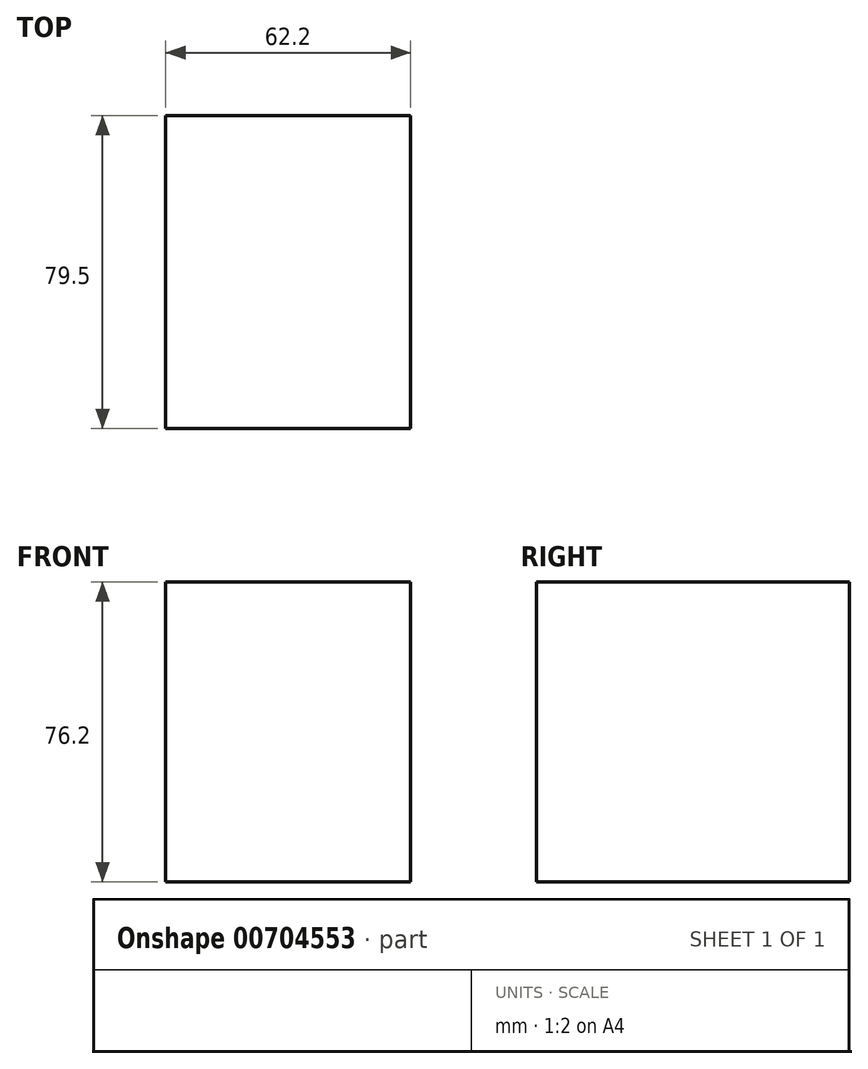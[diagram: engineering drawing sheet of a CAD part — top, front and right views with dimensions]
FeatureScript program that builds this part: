
annotation { "Feature Type Name" : "Feature", "Feature Type Description" : "" }
export const myFeature = defineFeature(function(context is Context, id is Id, definition is map)
    precondition{}
    {
        {
            var Q0;
            Q0=qCreatedBy(makeId("Top.planeOp"),FACE);
            var sketch = newSketch(context, id + "F0", { "sketchPlane" : qUnion([Q0])});
            skLineSegment(sketch, "E0.bottom", {"start": v(0, 79.5) * mm, "end": v(62.2, 79.5) * mm});
            skLineSegment(sketch, "E0.top", {"start": v(0, 0) * mm, "end": v(62.2, 0) * mm});
            skLineSegment(sketch, "E0.left", {"start": v(0, 79.5) * mm, "end": v(0, 0) * mm});
            skLineSegment(sketch, "E0.right", {"start": v(62.2, 79.5) * mm, "end": v(62.2, 0) * mm});
            skSolve(sketch);
        }
        {
            var Q0;
            Q0=makeQuery(id+"F0.imprint","IMPRINT",FACE,{"disambiguationData":[TD([[makeQuery(id+"F0.imprint","IMPRINT",EDGE,{"derivedFrom":sQuery(id+"F0.wireOp",EDGE,"E0.bottom")}),-1.0]])]});
            extrude(context, id + "F1", {"entities" : qUnion([Q0]), "depth" : 76.2 * mm, "offsetDistance" : 25.4 * mm});
        }
    });
